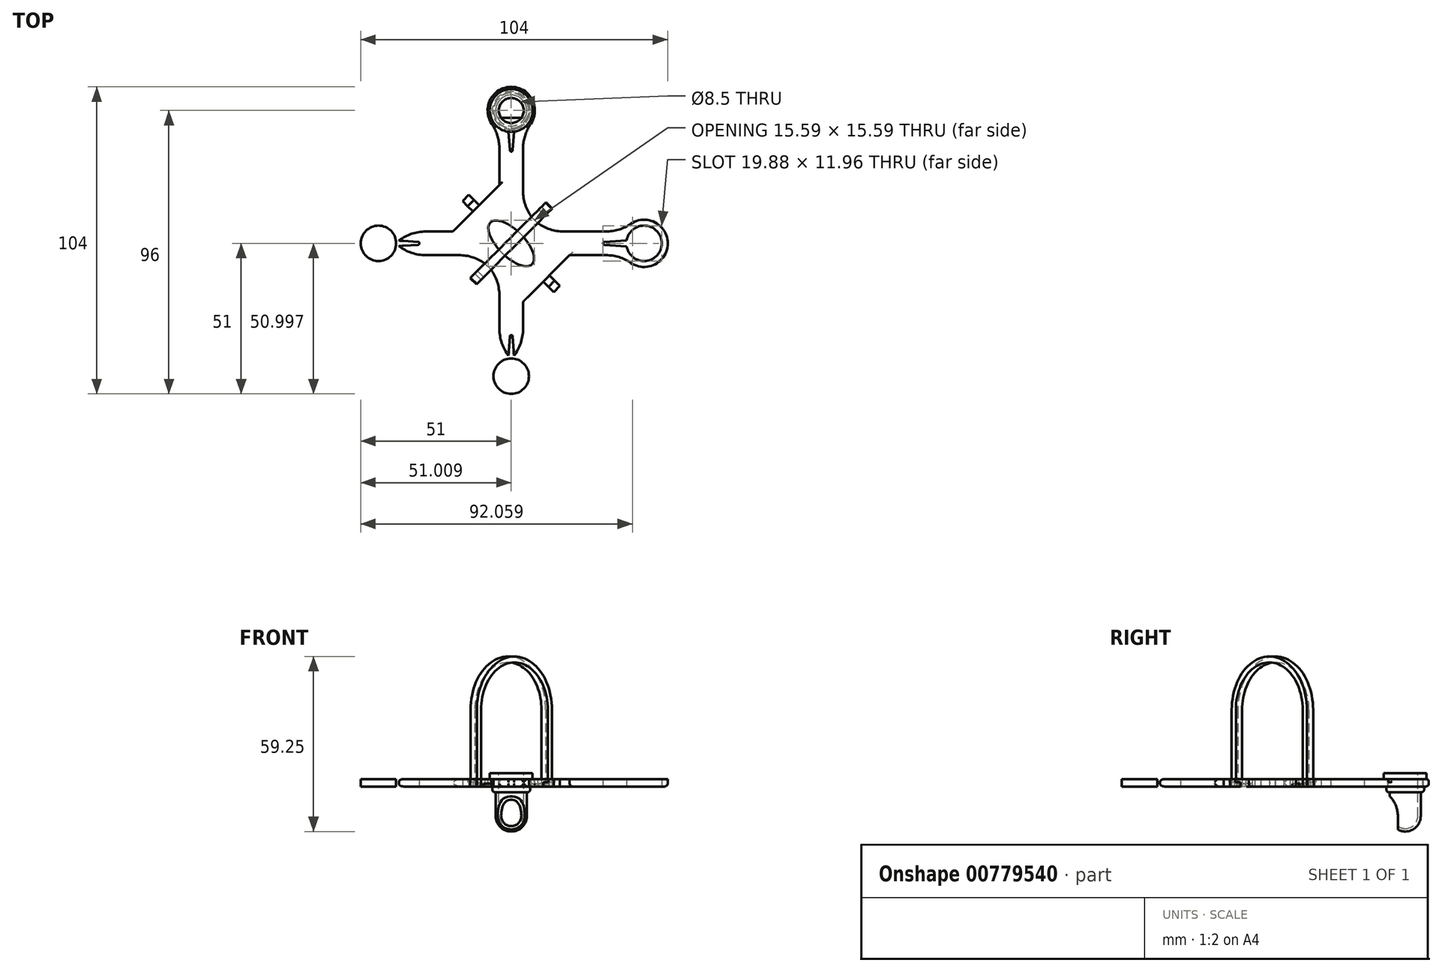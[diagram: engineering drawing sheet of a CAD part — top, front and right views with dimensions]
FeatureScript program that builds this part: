
annotation { "Feature Type Name" : "Feature", "Feature Type Description" : "" }
export const myFeature = defineFeature(function(context is Context, id is Id, definition is map)
    precondition{}
    {
        {
            var Q0;
            Q0=qCreatedBy(makeId("Top.planeOp"),FACE);
            var sketch = newSketch(context, id + "F0", { "sketchPlane" : qUnion([Q0])});
            skPoint(sketch, "E0.center", {"position": v(0, 45) * mm});
            skCircle(sketch, "E1", {"center": v(0, 45) * mm, "radius": 8 * mm});
            skPoint(sketch, "E2.MirrorP", {"position": v(0, -45) * mm});
            skPoint(sketch, "E3.center", {"position": v(-45, 0) * mm});
            skPoint(sketch, "E4.MirrorP", {"position": v(45, 0) * mm});
            skLineSegment(sketch, "E5.bottom", {"start": v(-4, 38.07) * mm, "end": v(4, 38.07) * mm});
            skLineSegment(sketch, "E5.top", {"start": v(-4, -38.07) * mm, "end": v(4, -38.07) * mm});
            skLineSegment(sketch, "E5.left", {"start": v(-4, 38.07) * mm, "end": v(-4, -38.07) * mm});
            skLineSegment(sketch, "E5.right", {"start": v(4, 38.07) * mm, "end": v(4, -38.07) * mm});
            skPoint(sketch, "E5.middle", {"position": v(0, 0) * mm});
            skLineSegment(sketch, "E6.bottom", {"start": v(-38.07, 4) * mm, "end": v(38.07, 4) * mm});
            skLineSegment(sketch, "E6.top", {"start": v(-38.07, -4) * mm, "end": v(38.07, -4) * mm});
            skLineSegment(sketch, "E6.left", {"start": v(-38.07, 4) * mm, "end": v(-38.07, -4) * mm});
            skLineSegment(sketch, "E6.right", {"start": v(38.07, 4) * mm, "end": v(38.07, -4) * mm});
            skCircle(sketch, "E7", {"center": v(0, 45) * mm, "radius": 6 * mm});
            skCircle(sketch, "E8.MirrorC", {"center": v(0, -45) * mm, "radius": 6 * mm});
            skLineSegment(sketch, "E9", {"start": v(-38.9, 38.9) * mm, "end": v(38.9, -38.9) * mm, "construction": true});
            skCircle(sketch, "E10.MirrorC", {"center": v(-45, 0) * mm, "radius": 6 * mm});
            skCircle(sketch, "E11.MirrorC", {"center": v(45, 0) * mm, "radius": 6 * mm});
            skCircle(sketch, "E12.MirrorC", {"center": v(0, -45) * mm, "radius": 8 * mm});
            skCircle(sketch, "E13.MirrorC", {"center": v(-45, 0) * mm, "radius": 8 * mm});
            skCircle(sketch, "E14.MirrorC", {"center": v(45, 0) * mm, "radius": 8 * mm});
            skLineSegment(sketch, "E15", {"start": v(1, 39.08) * mm, "end": v(0, 24.12) * mm});
            skLineSegment(sketch, "E16.MirrorCS", {"start": v(-1, 39.08) * mm, "end": v(0, 24.12) * mm});
            skLineSegment(sketch, "E17.MirrorCS", {"start": v(-1, -39.08) * mm, "end": v(0, -24.12) * mm});
            skLineSegment(sketch, "E18.MirrorCS", {"start": v(1, -39.08) * mm, "end": v(0, -24.12) * mm});
            skLineSegment(sketch, "E19.MirrorCS", {"start": v(-39.08, 1) * mm, "end": v(-24.12, 0) * mm});
            skLineSegment(sketch, "E20.MirrorCS", {"start": v(-39.08, -1) * mm, "end": v(-24.12, 0) * mm});
            skLineSegment(sketch, "E21.MirrorCS", {"start": v(39.08, 1) * mm, "end": v(24.12, 0) * mm});
            skLineSegment(sketch, "E22.MirrorCS", {"start": v(39.08, -1) * mm, "end": v(24.12, 0) * mm});
            skCircle(sketch, "E23", {"center": v(0, 31.62) * mm, "radius": 0.5 * mm});
            skCircle(sketch, "E24.MirrorC", {"center": v(0, -31.62) * mm, "radius": 0.5 * mm});
            skCircle(sketch, "E25.MirrorC", {"center": v(-31.62, 0) * mm, "radius": 0.5 * mm});
            skCircle(sketch, "E26.MirrorC", {"center": v(31.62, 0) * mm, "radius": 0.5 * mm});
            skLineSegment(sketch, "E27", {"start": v(34.68, 34.68) * mm, "end": v(-38.79, -38.79) * mm, "construction": true});
            skSolve(sketch);
        }
        {
            var Q0;
            {var subQ3=sQuery(id+"F0.wireOp",EDGE,"E15");var subQ5=sQuery(id+"F0.wireOp",EDGE,"E7");var subQ6=makeQuery(id+"F0.imprint","INTERSECT",VERTEX,{"derivedFrom":[subQ5,subQ3]});Q0=makeQuery(id+"F0.imprint","IMPRINT",FACE,{"disambiguationData":[TD([[makeQuery(id+"F0.imprint","IMPRINT",EDGE,{"disambiguationData":[TD([[subQ6,-1.0]])],"derivedFrom":subQ5}),-1.0]])]});}
            var Q1;
            {var subQ1=sQuery(id+"F0.wireOp",EDGE,"E1");var subQ3=sQuery(id+"F0.wireOp",EDGE,"E16.MirrorCS");var subQ4=makeQuery(id+"F0.imprint","INTERSECT",VERTEX,{"derivedFrom":[subQ1,subQ3]});Q1=makeQuery(id+"F0.imprint","IMPRINT",FACE,{"disambiguationData":[TD([[makeQuery(id+"F0.imprint","IMPRINT",EDGE,{"disambiguationData":[TD([[subQ4,1.0]])],"derivedFrom":subQ3}),-1.0]])]});}
            var Q2;
            {var subQ1=sQuery(id+"F0.wireOp",EDGE,"E1");var subQ3=sQuery(id+"F0.wireOp",EDGE,"E15");var subQ4=makeQuery(id+"F0.imprint","INTERSECT",VERTEX,{"derivedFrom":[subQ1,subQ3]});Q2=makeQuery(id+"F0.imprint","IMPRINT",FACE,{"disambiguationData":[TD([[makeQuery(id+"F0.imprint","IMPRINT",EDGE,{"disambiguationData":[TD([[subQ4,1.0]])],"derivedFrom":subQ3}),1.0]])]});}
            var Q3;
            {var subQ4=sQuery(id+"F0.wireOp",EDGE,"E6.bottom");var subQ8=sQuery(id+"F0.wireOp",EDGE,"E5.left");var subQ10=makeQuery(id+"F0.imprint","INTERSECT",VERTEX,{"derivedFrom":[subQ8,subQ4]});Q3=makeQuery(id+"F0.imprint","IMPRINT",FACE,{"disambiguationData":[TD([[makeQuery(id+"F0.imprint","IMPRINT",EDGE,{"disambiguationData":[TD([[subQ10,-1.0]])],"derivedFrom":subQ4}),1.0]])]});}
            var Q4;
            {var subQ0=sQuery(id+"F0.wireOp",EDGE,"E16.MirrorCS");var subQ1=sQuery(id+"F0.wireOp",EDGE,"E15");var subQ2=makeQuery(id+"F0.imprint","INTERSECT",VERTEX,{"derivedFrom":[subQ1,subQ0]});Q4=makeQuery(id+"F0.imprint","IMPRINT",FACE,{"disambiguationData":[TD([[makeQuery(id+"F0.imprint","IMPRINT",EDGE,{"disambiguationData":[TD([[subQ2,1.0]])],"derivedFrom":subQ1}),-1.0]])]});}
            var Q5;
            {var subQ4=sQuery(id+"F0.wireOp",EDGE,"E5.right");var subQ6=sQuery(id+"F0.wireOp",EDGE,"E6.bottom");var subQ8=makeQuery(id+"F0.imprint","INTERSECT",VERTEX,{"derivedFrom":[subQ4,subQ6]});Q5=makeQuery(id+"F0.imprint","IMPRINT",FACE,{"disambiguationData":[TD([[makeQuery(id+"F0.imprint","IMPRINT",EDGE,{"disambiguationData":[TD([[subQ8,-1.0]])],"derivedFrom":subQ4}),1.0]])]});}
            var Q6;
            {var subQ4=sQuery(id+"F0.wireOp",EDGE,"E21.MirrorCS");var subQ8=sQuery(id+"F0.wireOp",EDGE,"E11.MirrorC");var subQ10=makeQuery(id+"F0.imprint","INTERSECT",VERTEX,{"derivedFrom":[subQ8,subQ4]});Q6=makeQuery(id+"F0.imprint","IMPRINT",FACE,{"disambiguationData":[TD([[makeQuery(id+"F0.imprint","IMPRINT",EDGE,{"disambiguationData":[TD([[subQ10,1.0]])],"derivedFrom":subQ8}),-1.0]])]});}
            var Q7;
            {var subQ1=sQuery(id+"F0.wireOp",EDGE,"E6.right");var subQ3=sQuery(id+"F0.wireOp",EDGE,"E21.MirrorCS");var subQ4=makeQuery(id+"F0.imprint","INTERSECT",VERTEX,{"derivedFrom":[subQ1,subQ3]});Q7=makeQuery(id+"F0.imprint","IMPRINT",FACE,{"disambiguationData":[TD([[makeQuery(id+"F0.imprint","IMPRINT",EDGE,{"disambiguationData":[TD([[subQ4,-1.0]])],"derivedFrom":subQ3}),-1.0]])]});}
            var Q8;
            {var subQ1=sQuery(id+"F0.wireOp",EDGE,"E6.right");var subQ3=sQuery(id+"F0.wireOp",EDGE,"E22.MirrorCS");var subQ4=makeQuery(id+"F0.imprint","INTERSECT",VERTEX,{"derivedFrom":[subQ1,subQ3]});Q8=makeQuery(id+"F0.imprint","IMPRINT",FACE,{"disambiguationData":[TD([[makeQuery(id+"F0.imprint","IMPRINT",EDGE,{"disambiguationData":[TD([[subQ4,-1.0]])],"derivedFrom":subQ3}),1.0]])]});}
            var Q9;
            {var subQ0=sQuery(id+"F0.wireOp",EDGE,"E6.bottom");var subQ1=sQuery(id+"F0.wireOp",EDGE,"E5.left");var subQ2=makeQuery(id+"F0.imprint","INTERSECT",VERTEX,{"derivedFrom":[subQ1,subQ0]});Q9=makeQuery(id+"F0.imprint","IMPRINT",FACE,{"disambiguationData":[TD([[makeQuery(id+"F0.imprint","IMPRINT",EDGE,{"disambiguationData":[TD([[subQ2,-1.0]])],"derivedFrom":subQ1}),1.0]])]});}
            var Q10;
            {var subQ2=sQuery(id+"F0.wireOp",EDGE,"E6.bottom");var subQ8=sQuery(id+"F0.wireOp",EDGE,"E5.left");var subQ10=makeQuery(id+"F0.imprint","INTERSECT",VERTEX,{"derivedFrom":[subQ8,subQ2]});Q10=makeQuery(id+"F0.imprint","IMPRINT",FACE,{"disambiguationData":[TD([[makeQuery(id+"F0.imprint","IMPRINT",EDGE,{"disambiguationData":[TD([[subQ10,-1.0]])],"derivedFrom":subQ8}),-1.0]])]});}
            var Q11;
            {var subQ0=sQuery(id+"F0.wireOp",EDGE,"E22.MirrorCS");var subQ1=sQuery(id+"F0.wireOp",EDGE,"E21.MirrorCS");var subQ2=makeQuery(id+"F0.imprint","INTERSECT",VERTEX,{"derivedFrom":[subQ1,subQ0]});Q11=makeQuery(id+"F0.imprint","IMPRINT",FACE,{"disambiguationData":[TD([[makeQuery(id+"F0.imprint","IMPRINT",EDGE,{"disambiguationData":[TD([[subQ2,1.0]])],"derivedFrom":subQ1}),1.0]])]});}
            var Q12;
            {var subQ0=sQuery(id+"F0.wireOp",EDGE,"E18.MirrorCS");var subQ1=sQuery(id+"F0.wireOp",EDGE,"E17.MirrorCS");var subQ2=makeQuery(id+"F0.imprint","INTERSECT",VERTEX,{"derivedFrom":[subQ1,subQ0]});Q12=makeQuery(id+"F0.imprint","IMPRINT",FACE,{"disambiguationData":[TD([[makeQuery(id+"F0.imprint","IMPRINT",EDGE,{"disambiguationData":[TD([[subQ2,1.0]])],"derivedFrom":subQ1}),-1.0]])]});}
            var Q13;
            {var subQ1=sQuery(id+"F0.wireOp",EDGE,"E5.left");var subQ8=sQuery(id+"F0.wireOp",EDGE,"E6.top");var subQ9=makeQuery(id+"F0.imprint","INTERSECT",VERTEX,{"derivedFrom":[subQ1,subQ8]});Q13=makeQuery(id+"F0.imprint","IMPRINT",FACE,{"disambiguationData":[TD([[makeQuery(id+"F0.imprint","IMPRINT",EDGE,{"disambiguationData":[TD([[subQ9,-1.0]])],"derivedFrom":subQ8}),-1.0]])]});}
            var Q14;
            {var subQ1=sQuery(id+"F0.wireOp",EDGE,"E5.top");var subQ3=sQuery(id+"F0.wireOp",EDGE,"E18.MirrorCS");var subQ4=makeQuery(id+"F0.imprint","INTERSECT",VERTEX,{"derivedFrom":[subQ1,subQ3]});Q14=makeQuery(id+"F0.imprint","IMPRINT",FACE,{"disambiguationData":[TD([[makeQuery(id+"F0.imprint","IMPRINT",EDGE,{"disambiguationData":[TD([[subQ4,-1.0]])],"derivedFrom":subQ3}),-1.0]])]});}
            var Q15;
            {var subQ1=sQuery(id+"F0.wireOp",EDGE,"E5.top");var subQ3=sQuery(id+"F0.wireOp",EDGE,"E17.MirrorCS");var subQ4=makeQuery(id+"F0.imprint","INTERSECT",VERTEX,{"derivedFrom":[subQ1,subQ3]});Q15=makeQuery(id+"F0.imprint","IMPRINT",FACE,{"disambiguationData":[TD([[makeQuery(id+"F0.imprint","IMPRINT",EDGE,{"disambiguationData":[TD([[subQ4,-1.0]])],"derivedFrom":subQ3}),1.0]])]});}
            var Q16;
            {var subQ0=sQuery(id+"F0.wireOp",EDGE,"E17.MirrorCS");var subQ1=sQuery(id+"F0.wireOp",EDGE,"E8.MirrorC");var subQ2=makeQuery(id+"F0.imprint","INTERSECT",VERTEX,{"derivedFrom":[subQ1,subQ0]});Q16=makeQuery(id+"F0.imprint","IMPRINT",FACE,{"disambiguationData":[TD([[makeQuery(id+"F0.imprint","IMPRINT",EDGE,{"disambiguationData":[TD([[subQ2,1.0]])],"derivedFrom":subQ1}),1.0]])]});}
            var Q17;
            {var subQ4=sQuery(id+"F0.wireOp",EDGE,"E19.MirrorCS");var subQ5=sQuery(id+"F0.wireOp",EDGE,"E10.MirrorC");var subQ6=makeQuery(id+"F0.imprint","INTERSECT",VERTEX,{"derivedFrom":[subQ5,subQ4]});Q17=makeQuery(id+"F0.imprint","IMPRINT",FACE,{"disambiguationData":[TD([[makeQuery(id+"F0.imprint","IMPRINT",EDGE,{"disambiguationData":[TD([[subQ6,1.0]])],"derivedFrom":subQ5}),1.0]])]});}
            var Q18;
            {var subQ1=sQuery(id+"F0.wireOp",EDGE,"E6.left");var subQ3=sQuery(id+"F0.wireOp",EDGE,"E19.MirrorCS");var subQ4=makeQuery(id+"F0.imprint","INTERSECT",VERTEX,{"derivedFrom":[subQ1,subQ3]});Q18=makeQuery(id+"F0.imprint","IMPRINT",FACE,{"disambiguationData":[TD([[makeQuery(id+"F0.imprint","IMPRINT",EDGE,{"disambiguationData":[TD([[subQ4,-1.0]])],"derivedFrom":subQ3}),1.0]])]});}
            var Q19;
            {var subQ1=sQuery(id+"F0.wireOp",EDGE,"E6.left");var subQ3=sQuery(id+"F0.wireOp",EDGE,"E20.MirrorCS");var subQ4=makeQuery(id+"F0.imprint","INTERSECT",VERTEX,{"derivedFrom":[subQ1,subQ3]});Q19=makeQuery(id+"F0.imprint","IMPRINT",FACE,{"disambiguationData":[TD([[makeQuery(id+"F0.imprint","IMPRINT",EDGE,{"disambiguationData":[TD([[subQ4,-1.0]])],"derivedFrom":subQ3}),-1.0]])]});}
            var Q20;
            {var subQ0=sQuery(id+"F0.wireOp",EDGE,"E20.MirrorCS");var subQ1=sQuery(id+"F0.wireOp",EDGE,"E19.MirrorCS");var subQ2=makeQuery(id+"F0.imprint","INTERSECT",VERTEX,{"derivedFrom":[subQ1,subQ0]});Q20=makeQuery(id+"F0.imprint","IMPRINT",FACE,{"disambiguationData":[TD([[makeQuery(id+"F0.imprint","IMPRINT",EDGE,{"disambiguationData":[TD([[subQ2,1.0]])],"derivedFrom":subQ1}),-1.0]])]});}
            extrude(context, id + "F1", {"entities" : qUnion([Q0, Q1, Q2, Q3, Q4, Q5, Q6, Q7, Q8, Q9, Q10, Q11, Q12, Q13, Q14, Q15, Q16, Q17, Q18, Q19, Q20]), "depth" : 2.5 * mm, "offsetDistance" : 25 * mm});
        }
        {
            var Q0;
            Q0=qCreatedBy(makeId("Top.planeOp"),FACE);
            var sketch = newSketch(context, id + "F2", { "sketchPlane" : qUnion([Q0])});
            skLineSegment(sketch, "E28.bottom", {"start": v(-19.8, 4) * mm, "end": v(-4, 19.8) * mm});
            skLineSegment(sketch, "E28.top", {"start": v(4, -19.8) * mm, "end": v(19.8, -4) * mm});
            skLineSegment(sketch, "E28.left", {"start": v(-19.8, 4) * mm, "end": v(4, -19.8) * mm});
            skLineSegment(sketch, "E28.right", {"start": v(-4, 19.8) * mm, "end": v(19.8, -4) * mm});
            skPoint(sketch, "E28.middle", {"position": v(0, 0) * mm});
            skLineSegment(sketch, "E29.bottom", {"start": v(4.24, -18.38) * mm, "end": v(18.38, -4.24) * mm, "construction": true});
            skLineSegment(sketch, "E29.top", {"start": v(-18.38, 4.24) * mm, "end": v(-4.24, 18.38) * mm, "construction": true});
            skLineSegment(sketch, "E29.left", {"start": v(4.24, -18.38) * mm, "end": v(-18.38, 4.24) * mm, "construction": true});
            skLineSegment(sketch, "E29.right", {"start": v(18.38, -4.24) * mm, "end": v(-4.24, 18.38) * mm, "construction": true});
            skLineSegment(sketch, "E30", {"start": v(6.84, 8.96) * mm, "end": v(11.79, 13.9) * mm});
            skLineSegment(sketch, "E31", {"start": v(11.79, 13.9) * mm, "end": v(13.9, 11.79) * mm});
            skLineSegment(sketch, "E32", {"start": v(13.9, 11.79) * mm, "end": v(8.96, 6.84) * mm});
            skLineSegment(sketch, "E33.MirrorCS", {"start": v(-8.96, -6.84) * mm, "end": v(-13.9, -11.79) * mm});
            skLineSegment(sketch, "E34.MirrorCS", {"start": v(-11.79, -13.9) * mm, "end": v(-6.84, -8.96) * mm});
            skLineSegment(sketch, "E35.MirrorCS", {"start": v(-13.9, -11.79) * mm, "end": v(-11.79, -13.9) * mm});
            skLineSegment(sketch, "E36", {"start": v(9.31, 11.43) * mm, "end": v(11.43, 9.31) * mm});
            skLineSegment(sketch, "E37", {"start": v(-11.43, -9.31) * mm, "end": v(-9.31, -11.43) * mm});
            skLineSegment(sketch, "E38", {"start": v(-12.97, 10.83) * mm, "end": v(-16.5, 14.36) * mm});
            skLineSegment(sketch, "E39", {"start": v(-16.5, 14.36) * mm, "end": v(-14.38, 16.48) * mm});
            skLineSegment(sketch, "E40", {"start": v(-14.38, 16.48) * mm, "end": v(-10.85, 12.95) * mm});
            skLineSegment(sketch, "E41", {"start": v(-12.62, 14.72) * mm, "end": v(-14.74, 12.6) * mm});
            skLineSegment(sketch, "E42.MirrorCS", {"start": v(16.48, -14.38) * mm, "end": v(12.95, -10.85) * mm});
            skLineSegment(sketch, "E43.MirrorCS", {"start": v(10.83, -12.97) * mm, "end": v(14.36, -16.5) * mm});
            skLineSegment(sketch, "E44.MirrorCS", {"start": v(14.36, -16.5) * mm, "end": v(16.48, -14.38) * mm});
            skLineSegment(sketch, "E45.MirrorCS", {"start": v(14.72, -12.62) * mm, "end": v(12.6, -14.74) * mm});
            skSolve(sketch);
        }
        {
            var Q0;
            Q0=qSketchRegion(id+"F2",true);
            extrude(context, id + "F3", {"entities" : qUnion([Q0]), "operationType" : NewBodyOperationType.ADD, "depth" : 2.5 * mm, "offsetDistance" : 25 * mm});
        }
        {
            var Q0;
            {var subQ0=sQuery(id+"F0.wireOp",EDGE,"E5.left");var subQ2=sQuery(id+"F0.wireOp",EDGE,"E1");var subQ3=sQuery(id+"F0.wireOp",EDGE,"E6.bottom");var subQ5=sQuery(id+"F0.wireOp",EDGE,"51bbf768-7248-469b-8c03-81a92e2fee1e4.MirrorC");var subQ6=sQuery(id+"F0.wireOp",EDGE,"51bbf768-7248-469b-8c03-81a92e2fee1e3.MirrorC");var subQ7=sQuery(id+"F0.wireOp",EDGE,"51bbf768-7248-469b-8c03-81a92e2fee1e2.MirrorC");var subQ8=sQuery(id+"F0.wireOp",EDGE,"51bbf768-7248-469b-8c03-81a92e2fee1e1.MirrorC");var subQ9=sQuery(id+"F0.wireOp",EDGE,"51bbf768-7248-469b-8c03-81a92e2fee1e0.MirrorC");var subQ10=sQuery(id+"F0.wireOp",EDGE,"19e26025-abd8-4f06-8e8c-6a666a63a616");var subQ11=sQuery(id+"F0.wireOp",EDGE,"598c6ef1-5939-428d-88fe-4b21ed39706e.1.3.0");var subQ12=sQuery(id+"F0.wireOp",EDGE,"E3.2.0");var subQ13=sQuery(id+"F0.wireOp",EDGE,"E3.1.0");var subQ14=sQuery(id+"F0.wireOp",EDGE,"c63fb3b6-9377-47fa-ba11-29589a2d911d");var subQ15=sQuery(id+"F0.wireOp",EDGE,"E0.2.0");var subQ16=sQuery(id+"F0.wireOp",EDGE,"E0.1.0");var subQ17=sQuery(id+"F0.wireOp",EDGE,"1841d06c-6167-486a-ac26-2bc6ea0ff5a3.1.3.0");var subQ19=sQuery(id+"F0.wireOp",EDGE,"20bb631d-0421-4e81-8fba-f625033d7a898.MirrorC");var subQ20=sQuery(id+"F0.wireOp",EDGE,"E6.top");var subQ22=sQuery(id+"F0.wireOp",EDGE,"jg3JzTFg-ilfI-jJIB-Kd6Z-DIGPSq1nITlw");var subQ23=sQuery(id+"F0.wireOp",EDGE,"20bb631d-0421-4e81-8fba-f625033d7a890.MirrorC");var subQ24=sQuery(id+"F0.wireOp",EDGE,"20bb631d-0421-4e81-8fba-f625033d7a891.MirrorC");var subQ25=sQuery(id+"F0.wireOp",EDGE,"20bb631d-0421-4e81-8fba-f625033d7a892.MirrorC");var subQ26=sQuery(id+"F0.wireOp",EDGE,"20bb631d-0421-4e81-8fba-f625033d7a893.MirrorC");var subQ27=sQuery(id+"F0.wireOp",EDGE,"E5.right");var subQ32=sQuery(id+"F2.wireOp",EDGE,"UVMeGlA9-Bkmn-TeG9-sZP4-qDwB2kEt46mr.bottom");var subQ33=sQuery(id+"F2.wireOp",EDGE,"UVMeGlA9-Bkmn-TeG9-sZP4-qDwB2kEt46mr.top");var subQ34=sQuery(id+"F2.wireOp",EDGE,"UVMeGlA9-Bkmn-TeG9-sZP4-qDwB2kEt46mr.left");var subQ35=sQuery(id+"F2.wireOp",EDGE,"UVMeGlA9-Bkmn-TeG9-sZP4-qDwB2kEt46mr.right");Q0=makeQuery(id+"FhcVAunL5KojDzv_1.boolean.opBoolean","SPLIT",FACE,{"disambiguationData":[TD([makeQuery(id+"F1.opExtrude","SWEPT_FACE",FACE,{"disambiguationData":[OSD([subQ22])]})])],"derivedFrom":makeQuery(id+"F3.boolean.opBoolean","MERGE",FACE,{"derivedFrom":[makeQuery(id+"F1.opExtrude","CAP_FACE",FACE,{"disambiguationData":[OSD([subQ22,subQ16,subQ15,subQ17,subQ2,subQ23,subQ24,subQ25,subQ26,subQ19,subQ14,subQ13,subQ12,subQ11,subQ10,subQ9,subQ8,subQ7,subQ6,subQ5,subQ0,subQ27,subQ3,subQ20])],"isStart":false}),makeQuery(id+"F3.opExtrude","CAP_FACE",FACE,{"disambiguationData":[OSD([subQ32,subQ33,subQ34,subQ35])],"isStart":false})]})});}
            var sketch = newSketch(context, id + "F4", { "sketchPlane" : qUnion([Q0])});
            skEllipse(sketch, "E46", {"center": v(0, 0) * mm, "majorRadius": 10 * mm, "minorRadius": 4.5 * mm, "majorAxis": v(-0.7, 0.7)});
            skSolve(sketch);
        }
        {
            var Q0;
            Q0=makeQuery(id+"F4.imprint","IMPRINT",FACE,{"disambiguationData":[TD([[makeQuery(id+"F4.imprint","IMPRINT",EDGE,{"derivedFrom":sQuery(id+"F4.wireOp",EDGE,"E46")}),1.0]])]});
            extrude(context, id + "F5", {"entities" : qUnion([Q0]), "operationType" : NewBodyOperationType.REMOVE, "endBound" : BoundingType.UP_TO_NEXT, "oppositeDirection" : true, "depth" : 25 * mm, "offsetDistance" : 25 * mm});
        }
        {
            var Q0;
            Q0=makeQuery(id+"F3.opExtrude","SWEPT_EDGE",EDGE,{"disambiguationData":[OSD([sQuery(id+"F2.wireOp",EDGE,"E28.top"),sQuery(id+"F2.wireOp",EDGE,"E28.right")])]});
            var Q1;
            Q1=makeQuery(id+"F3.opExtrude","SWEPT_EDGE",EDGE,{"disambiguationData":[OSD([sQuery(id+"F2.wireOp",EDGE,"E28.top"),sQuery(id+"F2.wireOp",EDGE,"E28.left")])]});
            var Q2;
            {var subQ0=sQuery(id+"F0.wireOp",EDGE,"E5.left");Q2=makeQuery(id+"F3.boolean.opBoolean","INTERSECT",EDGE,{"derivedFrom":[makeQuery(id+"F1.opExtrude","SWEPT_FACE",FACE,{"disambiguationData":[OSD([subQ0]),TDD([makeQuery(id+"F0.imprint","IMPRINT",EDGE,{"disambiguationData":[TD([[makeQuery(id+"F0.imprint","INTERSECT",VERTEX,{"derivedFrom":[subQ0,sQuery(id+"F0.wireOp",EDGE,"E6.top")]}),-1.0]])],"derivedFrom":subQ0})])]}),makeQuery(id+"F3.opExtrude","SWEPT_FACE",FACE,{"disambiguationData":[OSD([sQuery(id+"F2.wireOp",EDGE,"E28.left")])]})]});}
            var Q3;
            {var subQ0=sQuery(id+"F0.wireOp",EDGE,"E6.top");Q3=makeQuery(id+"F3.boolean.opBoolean","INTERSECT",EDGE,{"derivedFrom":[makeQuery(id+"F1.opExtrude","SWEPT_FACE",FACE,{"disambiguationData":[OSD([subQ0]),TDD([makeQuery(id+"F0.imprint","IMPRINT",EDGE,{"disambiguationData":[TD([[makeQuery(id+"F0.imprint","INTERSECT",VERTEX,{"derivedFrom":[sQuery(id+"F0.wireOp",EDGE,"E5.left"),subQ0]}),1.0]])],"derivedFrom":subQ0})])]}),makeQuery(id+"F3.opExtrude","SWEPT_FACE",FACE,{"disambiguationData":[OSD([sQuery(id+"F2.wireOp",EDGE,"E28.left")])]})]});}
            var Q4;
            {var subQ0=sQuery(id+"F0.wireOp",EDGE,"E6.bottom");Q4=makeQuery(id+"F3.boolean.opBoolean","INTERSECT",EDGE,{"derivedFrom":[makeQuery(id+"F1.opExtrude","SWEPT_FACE",FACE,{"disambiguationData":[OSD([subQ0]),TDD([makeQuery(id+"F0.imprint","IMPRINT",EDGE,{"disambiguationData":[TD([[makeQuery(id+"F0.imprint","INTERSECT",VERTEX,{"derivedFrom":[sQuery(id+"F0.wireOp",EDGE,"E5.right"),subQ0]}),-1.0]])],"derivedFrom":subQ0})])]}),makeQuery(id+"F3.opExtrude","SWEPT_FACE",FACE,{"disambiguationData":[OSD([sQuery(id+"F2.wireOp",EDGE,"E28.right")])]})]});}
            var Q5;
            {var subQ0=sQuery(id+"F0.wireOp",EDGE,"E5.right");Q5=makeQuery(id+"F3.boolean.opBoolean","INTERSECT",EDGE,{"derivedFrom":[makeQuery(id+"F1.opExtrude","SWEPT_FACE",FACE,{"disambiguationData":[OSD([subQ0]),TDD([makeQuery(id+"F0.imprint","IMPRINT",EDGE,{"disambiguationData":[TD([[makeQuery(id+"F0.imprint","INTERSECT",VERTEX,{"derivedFrom":[subQ0,sQuery(id+"F0.wireOp",EDGE,"E6.bottom")]}),1.0]])],"derivedFrom":subQ0})])]}),makeQuery(id+"F3.opExtrude","SWEPT_FACE",FACE,{"disambiguationData":[OSD([sQuery(id+"F2.wireOp",EDGE,"E28.right")])]})]});}
            var Q6;
            Q6=makeQuery(id+"F3.opExtrude","SWEPT_EDGE",EDGE,{"disambiguationData":[OSD([sQuery(id+"F2.wireOp",EDGE,"E28.bottom"),sQuery(id+"F2.wireOp",EDGE,"E28.right")])]});
            var Q7;
            Q7=makeQuery(id+"F3.opExtrude","SWEPT_EDGE",EDGE,{"disambiguationData":[OSD([sQuery(id+"F2.wireOp",EDGE,"E28.bottom"),sQuery(id+"F2.wireOp",EDGE,"E28.left")])]});
            var Q8;
            Q8=makeQuery(id+"F1.opExtrude","SWEPT_EDGE",EDGE,{"disambiguationData":[OSD([sQuery(id+"F0.wireOp",EDGE,"E5.top"),sQuery(id+"F0.wireOp",EDGE,"E5.left"),sQuery(id+"F0.wireOp",EDGE,"E12.MirrorC")])]});
            var Q9;
            Q9=makeQuery(id+"F1.opExtrude","SWEPT_EDGE",EDGE,{"disambiguationData":[OSD([sQuery(id+"F0.wireOp",EDGE,"E5.top"),sQuery(id+"F0.wireOp",EDGE,"E5.right"),sQuery(id+"F0.wireOp",EDGE,"E12.MirrorC")])]});
            var Q10;
            Q10=makeQuery(id+"F1.opExtrude","SWEPT_EDGE",EDGE,{"disambiguationData":[OSD([sQuery(id+"F0.wireOp",EDGE,"E6.top"),sQuery(id+"F0.wireOp",EDGE,"E6.right"),sQuery(id+"F0.wireOp",EDGE,"E14.MirrorC")])]});
            var Q11;
            Q11=makeQuery(id+"F1.opExtrude","SWEPT_EDGE",EDGE,{"disambiguationData":[OSD([sQuery(id+"F0.wireOp",EDGE,"E6.bottom"),sQuery(id+"F0.wireOp",EDGE,"E6.right"),sQuery(id+"F0.wireOp",EDGE,"E14.MirrorC")])]});
            var Q12;
            Q12=makeQuery(id+"F1.opExtrude","SWEPT_EDGE",EDGE,{"disambiguationData":[OSD([sQuery(id+"F0.wireOp",EDGE,"E1"),sQuery(id+"F0.wireOp",EDGE,"E5.bottom"),sQuery(id+"F0.wireOp",EDGE,"E5.right")])]});
            var Q13;
            Q13=makeQuery(id+"F1.opExtrude","SWEPT_EDGE",EDGE,{"disambiguationData":[OSD([sQuery(id+"F0.wireOp",EDGE,"E1"),sQuery(id+"F0.wireOp",EDGE,"E5.bottom"),sQuery(id+"F0.wireOp",EDGE,"E5.left")])]});
            var Q14;
            Q14=makeQuery(id+"F1.opExtrude","SWEPT_EDGE",EDGE,{"disambiguationData":[OSD([sQuery(id+"F0.wireOp",EDGE,"E6.top"),sQuery(id+"F0.wireOp",EDGE,"E6.left"),sQuery(id+"F0.wireOp",EDGE,"E13.MirrorC")])]});
            var Q15;
            Q15=makeQuery(id+"F1.opExtrude","SWEPT_EDGE",EDGE,{"disambiguationData":[OSD([sQuery(id+"F0.wireOp",EDGE,"E6.bottom"),sQuery(id+"F0.wireOp",EDGE,"E6.left"),sQuery(id+"F0.wireOp",EDGE,"E13.MirrorC")])]});
            fillet(context, id + "F6", {"entities" : qUnion([Q0, Q1, Q2, Q3, Q4, Q5, Q6, Q7, Q8, Q9, Q10, Q11, Q12, Q13, Q14, Q15]), "radius" : 15 * mm, "tangentPropagation" : true, "allowEdgeOverflow" : false});
        }
        {
            var Q0;
            {var subQ5=sQuery(id+"F2.wireOp",EDGE,"E41");Q0=makeQuery(id+"F2.imprint","IMPRINT",FACE,{"disambiguationData":[TD([[makeQuery(id+"F2.imprint","IMPRINT",EDGE,{"derivedFrom":subQ5}),1.0]])]});}
            var Q1;
            {var subQ5=sQuery(id+"F2.wireOp",EDGE,"E45.MirrorCS");Q1=makeQuery(id+"F2.imprint","IMPRINT",FACE,{"disambiguationData":[TD([[makeQuery(id+"F2.imprint","IMPRINT",EDGE,{"derivedFrom":subQ5}),-1.0]])]});}
            extrude(context, id + "F7", {"entities" : qUnion([Q0, Q1]), "operationType" : NewBodyOperationType.REMOVE, "depth" : 3 * mm, "offsetDistance" : 25 * mm, "hasSecondDirection" : true, "secondDirectionOppositeDirection" : false, "secondDirectionDepth" : 1.5 * mm});
        }
        {
            var Q0;
            {var subQ0=sQuery(id+"F2.wireOp",EDGE,"E28.bottom");var subQ1=sQuery(id+"F2.wireOp",EDGE,"E34.MirrorCS");var subQ2=sQuery(id+"F2.wireOp",EDGE,"E28.left");var subQ3=sQuery(id+"F0.wireOp",EDGE,"E14.MirrorC");var subQ4=sQuery(id+"F2.wireOp",EDGE,"E32");var subQ5=sQuery(id+"F0.wireOp",EDGE,"E13.MirrorC");var subQ6=sQuery(id+"F2.wireOp",EDGE,"E30");var subQ7=sQuery(id+"F0.wireOp",EDGE,"E12.MirrorC");var subQ8=sQuery(id+"F2.wireOp",EDGE,"E35.MirrorCS");var subQ9=sQuery(id+"F2.wireOp",EDGE,"E33.MirrorCS");var subQ10=sQuery(id+"F2.wireOp",EDGE,"E31");var subQ11=sQuery(id+"F2.wireOp",EDGE,"E28.right");var subQ12=sQuery(id+"F2.wireOp",EDGE,"E28.top");var subQ13=sQuery(id+"F0.wireOp",EDGE,"E11.MirrorC");var subQ14=sQuery(id+"F0.wireOp",EDGE,"E10.MirrorC");var subQ15=sQuery(id+"F0.wireOp",EDGE,"E8.MirrorC");var subQ16=sQuery(id+"F0.wireOp",EDGE,"E7");var subQ17=sQuery(id+"F0.wireOp",EDGE,"E6.top");var subQ18=sQuery(id+"F0.wireOp",EDGE,"E6.bottom");var subQ19=sQuery(id+"F0.wireOp",EDGE,"E5.right");var subQ20=sQuery(id+"F0.wireOp",EDGE,"E5.left");var subQ21=sQuery(id+"F0.wireOp",EDGE,"E1");var subQ22=makeQuery(id+"F3.boolean.opBoolean","MERGE",FACE,{"derivedFrom":[makeQuery(id+"F1.opExtrude","CAP_FACE",FACE,{"disambiguationData":[OSD([subQ21,subQ20,subQ19,subQ18,subQ17,subQ16,subQ15,subQ14,subQ13,subQ7,subQ5,subQ3])],"isStart":false}),makeQuery(id+"F3.opExtrude","CAP_FACE",FACE,{"disambiguationData":[OSD([subQ0,subQ12,subQ2,subQ11,subQ6,subQ10,subQ4,subQ9,subQ1,subQ8])],"isStart":false})]});Q0=makeQuery(id+"F7.boolean.opBoolean","SPLIT",FACE,{"disambiguationData":[TD([makeQuery(id+"F1.opExtrude","SWEPT_FACE",FACE,{"disambiguationData":[OSD([subQ16])]})])],"derivedFrom":subQ22});}
            var sketch = newSketch(context, id + "F8", { "sketchPlane" : qUnion([Q0])});
            skPoint(sketch, "E47.centerSnap0", {"position": v(0, 53) * mm});
            skCircle(sketch, "E48", {"center": v(0, 45) * mm, "radius": 5.9 * mm});
            skCircle(sketch, "E49", {"center": v(0, 45) * mm, "radius": 7.25 * mm});
            skCircle(sketch, "E50", {"center": v(0, 45) * mm, "radius": 4.25 * mm});
            skCircle(sketch, "E51", {"center": v(0, 45) * mm, "radius": 6.4 * mm});
            skSolve(sketch);
        }
        {
            var Q0;
            Q0=makeQuery(id+"F8.imprint","IMPRINT",FACE,{"disambiguationData":[TD([[makeQuery(id+"F8.imprint","IMPRINT",EDGE,{"derivedFrom":sQuery(id+"F8.wireOp",EDGE,"E48")}),1.0]])]});
            extrude(context, id + "F9", {"entities" : qUnion([Q0]), "oppositeDirection" : true, "depth" : 4.5 * mm, "offsetDistance" : 25 * mm});
        }
        {
            var Q0;
            Q0=makeQuery(id+"F8.imprint","IMPRINT",FACE,{"disambiguationData":[TD([[makeQuery(id+"F8.imprint","IMPRINT",EDGE,{"derivedFrom":sQuery(id+"F8.wireOp",EDGE,"E48")}),1.0]])]});
            var Q1;
            {var subQ5=makeQuery(id+"F1.opExtrude","CAP_EDGE",EDGE,{"disambiguationData":[OSD([sQuery(id+"F0.wireOp",EDGE,"E7")])],"isStart":false});Q1=makeQuery(id+"F8.imprint","IMPRINT",FACE,{"disambiguationData":[TD([[makeQuery(id+"F8.imprint","IMPRINT",EDGE,{"derivedFrom":subQ5}),-1.0]])]});}
            var Q2;
            Q2=makeQuery(id+"F8.imprint","IMPRINT",FACE,{"disambiguationData":[TD([[makeQuery(id+"F8.imprint","IMPRINT",EDGE,{"derivedFrom":sQuery(id+"F8.wireOp",EDGE,"E48")}),-1.0]])]});
            var Q3;
            {var subQ0=sQuery(id+"F8.wireOp",EDGE,"E49");var subQ1=makeQuery(id+"F1.opExtrude","CAP_EDGE",EDGE,{"disambiguationData":[OSD([sQuery(id+"F0.wireOp",EDGE,"E15")])],"isStart":false});var subQ2=makeQuery(id+"F8.imprint","INTERSECT",VERTEX,{"derivedFrom":[subQ1,subQ0]});Q3=makeQuery(id+"F8.imprint","IMPRINT",FACE,{"disambiguationData":[TD([[makeQuery(id+"F8.imprint","IMPRINT",EDGE,{"disambiguationData":[TD([[subQ2,-1.0]])],"derivedFrom":subQ0}),1.0]])]});}
            var Q4;
            {var subQ0=sQuery(id+"F8.wireOp",EDGE,"E49");var subQ1=makeQuery(id+"F1.opExtrude","CAP_EDGE",EDGE,{"disambiguationData":[OSD([sQuery(id+"F0.wireOp",EDGE,"E15")])],"isStart":false});var subQ2=makeQuery(id+"F8.imprint","INTERSECT",VERTEX,{"derivedFrom":[subQ1,subQ0]});Q4=makeQuery(id+"F8.imprint","IMPRINT",FACE,{"disambiguationData":[TD([[makeQuery(id+"F8.imprint","IMPRINT",EDGE,{"disambiguationData":[TD([[subQ2,1.0]])],"derivedFrom":subQ0}),1.0]])]});}
            extrude(context, id + "F10", {"entities" : qUnion([Q0, Q1, Q2, Q3, Q4]), "operationType" : NewBodyOperationType.ADD, "depth" : 2 * mm, "offsetDistance" : 25 * mm});
        }
        {
            var Q0;
            {var subQ5=makeQuery(id+"F1.opExtrude","CAP_EDGE",EDGE,{"disambiguationData":[OSD([sQuery(id+"F0.wireOp",EDGE,"E7")])],"isStart":false});Q0=makeQuery(id+"F8.imprint","IMPRINT",FACE,{"disambiguationData":[TD([[makeQuery(id+"F8.imprint","IMPRINT",EDGE,{"derivedFrom":subQ5}),-1.0]])]});}
            var Q1;
            Q1=makeQuery(id+"F8.imprint","IMPRINT",FACE,{"disambiguationData":[TD([[makeQuery(id+"F8.imprint","IMPRINT",EDGE,{"derivedFrom":sQuery(id+"F8.wireOp",EDGE,"E48")}),-1.0]])]});
            extrude(context, id + "F11", {"entities" : qUnion([Q0, Q1]), "operationType" : NewBodyOperationType.ADD, "oppositeDirection" : true, "depth" : 4.5 * mm, "offsetDistance" : 25 * mm, "hasSecondDirection" : true, "secondDirectionOppositeDirection" : true, "secondDirectionDepth" : 2.5 * mm});
        }
        {
            var Q0;
            Q0=qCreatedBy(makeId("Right.planeOp"),FACE);
            var sketch = newSketch(context, id + "F12", { "sketchPlane" : qUnion([Q0])});
            skArc(sketch, "E52", {"start": v(40.75, -10) * mm, "mid": v(42, -13) * mm, "end": v(45, -14.25) * mm});
            skLineSegment(sketch, "E53", {"start": v(40.75, -2) * mm, "end": v(40.75, -10) * mm});
            skArc(sketch, "E54.0", {"start": v(39.75, -10) * mm, "mid": v(41.29, -13.71) * mm, "end": v(45, -15.25) * mm});
            skLineSegment(sketch, "E54.1", {"start": v(39.75, -2) * mm, "end": v(39.75, -10) * mm});
            skLineSegment(sketch, "E55", {"start": v(45, -14.25) * mm, "end": v(45, -15.25) * mm});
            skLineSegment(sketch, "E56", {"start": v(45, -15.25) * mm, "end": v(45, 0) * mm, "construction": true});
            skLineSegment(sketch, "E57", {"start": v(39.75, -2) * mm, "end": v(40.75, -2) * mm});
            skSolve(sketch);
        }
        {
            var Q0;
            {var subQ0=sQuery(id+"F0.wireOp",EDGE,"E5.right");Q0=makeQuery(id+"F1.opExtrude","SWEPT_FACE",FACE,{"disambiguationData":[OSD([subQ0]),TDD([makeQuery(id+"F0.imprint","IMPRINT",EDGE,{"disambiguationData":[TD([[makeQuery(id+"F0.imprint","INTERSECT",VERTEX,{"derivedFrom":[subQ0,sQuery(id+"F0.wireOp",EDGE,"E6.top")]}),-1.0]])],"derivedFrom":subQ0})])]});}
            var Q1;
            {var subQ0=sQuery(id+"F0.wireOp",EDGE,"E5.left");Q1=makeQuery(id+"F1.opExtrude","SWEPT_FACE",FACE,{"disambiguationData":[OSD([subQ0]),TDD([makeQuery(id+"F0.imprint","IMPRINT",EDGE,{"disambiguationData":[TD([[makeQuery(id+"F0.imprint","INTERSECT",VERTEX,{"derivedFrom":[subQ0,sQuery(id+"F0.wireOp",EDGE,"E6.top")]}),-1.0]])],"derivedFrom":subQ0})])]});}
            var Q2;
            {var subQ0=sQuery(id+"F0.wireOp",EDGE,"E6.top");Q2=makeQuery(id+"F1.opExtrude","SWEPT_FACE",FACE,{"disambiguationData":[OSD([subQ0]),TDD([makeQuery(id+"F0.imprint","IMPRINT",EDGE,{"disambiguationData":[TD([[makeQuery(id+"F0.imprint","INTERSECT",VERTEX,{"derivedFrom":[sQuery(id+"F0.wireOp",EDGE,"E5.left"),subQ0]}),1.0]])],"derivedFrom":subQ0})])]});}
            var Q3;
            {var subQ0=sQuery(id+"F0.wireOp",EDGE,"E6.bottom");Q3=makeQuery(id+"F1.opExtrude","SWEPT_FACE",FACE,{"disambiguationData":[OSD([subQ0]),TDD([makeQuery(id+"F0.imprint","IMPRINT",EDGE,{"disambiguationData":[TD([[makeQuery(id+"F0.imprint","INTERSECT",VERTEX,{"derivedFrom":[sQuery(id+"F0.wireOp",EDGE,"E5.left"),subQ0]}),1.0]])],"derivedFrom":subQ0})])]});}
            var Q4;
            {var subQ0=sQuery(id+"F0.wireOp",EDGE,"E5.right");Q4=makeQuery(id+"F1.opExtrude","SWEPT_FACE",FACE,{"disambiguationData":[OSD([subQ0]),TDD([makeQuery(id+"F0.imprint","IMPRINT",EDGE,{"disambiguationData":[TD([[makeQuery(id+"F0.imprint","INTERSECT",VERTEX,{"derivedFrom":[subQ0,sQuery(id+"F0.wireOp",EDGE,"E6.bottom")]}),1.0]])],"derivedFrom":subQ0})])]});}
            var Q5;
            {var subQ0=sQuery(id+"F0.wireOp",EDGE,"E6.bottom");Q5=makeQuery(id+"F1.opExtrude","CAP_EDGE",EDGE,{"disambiguationData":[OSD([subQ0]),TDD([makeQuery(id+"F0.imprint","IMPRINT",EDGE,{"disambiguationData":[TD([[makeQuery(id+"F0.imprint","INTERSECT",VERTEX,{"derivedFrom":[sQuery(id+"F0.wireOp",EDGE,"E5.right"),subQ0]}),-1.0]])],"derivedFrom":subQ0})])],"isStart":true});}
            var Q6;
            Q6=makeQuery(id+"F5.boolean.opBoolean","COPY",FACE,{"derivedFrom":makeQuery(id+"F5.opExtrude","SWEPT_FACE",FACE,{"disambiguationData":[OSD([sQuery(id+"F4.wireOp",EDGE,"E46")])]})});
            var Q7;
            Q7=makeQuery(id+"F11.opExtrude","CAP_EDGE",EDGE,{"disambiguationData":[OSD([sQuery(id+"F8.wireOp",EDGE,"E51")])],"isStart":false});
            var Q8;
            Q8=makeQuery(id+"F11.opExtrude","CAP_EDGE",EDGE,{"disambiguationData":[OSD([sQuery(id+"F8.wireOp",EDGE,"E48")])],"isStart":true});
            fillet(context, id + "F13", {"entities" : qUnion([Q0, Q1, Q2, Q3, Q4, Q5, Q6, Q7, Q8]), "radius" : 1 * mm, "tangentPropagation" : true, "allowEdgeOverflow" : false});
        }
        {
            var Q0;
            Q0=makeQuery(id+"F12.imprint","IMPRINT",FACE,{"disambiguationData":[TD([[makeQuery(id+"F12.imprint","IMPRINT",EDGE,{"derivedFrom":sQuery(id+"F12.wireOp",EDGE,"E52")}),-1.0]])]});
            var Q1;
            Q1=sQuery(id+"F12.wireOp",EDGE,"E56");
            revolve(context, id + "F14", {"operationType" : NewBodyOperationType.ADD, "surfaceOperationType" : NewSurfaceOperationType.NEW, "entities" : qUnion([Q0]), "axis" : qUnion([Q1]), "revolveType" : RevolveType.FULL});
        }
        {
            var Q0;
            {var subQ5=sQuery(id+"F2.wireOp",EDGE,"E37");Q0=makeQuery(id+"F2.imprint","IMPRINT",FACE,{"disambiguationData":[TD([[makeQuery(id+"F2.imprint","IMPRINT",EDGE,{"derivedFrom":subQ5}),1.0]])]});}
            var Q1;
            {var subQ5=sQuery(id+"F2.wireOp",EDGE,"E36");Q1=makeQuery(id+"F2.imprint","IMPRINT",FACE,{"disambiguationData":[TD([[makeQuery(id+"F2.imprint","IMPRINT",EDGE,{"derivedFrom":subQ5}),-1.0]])]});}
            extrude(context, id + "F15", {"entities" : qUnion([Q0, Q1]), "operationType" : NewBodyOperationType.REMOVE, "depth" : 1 * mm, "offsetDistance" : 25 * mm});
        }
        {
            var Q0;
            Q0=sQuery(id+"F0.wireOp",EDGE,"E9");
            cPlane(context, id + "F16", {"entities" : qUnion([Q0]), "cplaneType" : CPlaneType.MID_PLANE, "offset" : 25 * mm, "width" : 150 * mm, "height" : 150 * mm});
        }
        {
            var Q0;
            Q0=qCreatedBy(id+"F16.planeOp",FACE);
            var sketch = newSketch(context, id + "F17", { "sketchPlane" : qUnion([Q0])});
            skArc(sketch, "E58", {"start": v(16, 26) * mm, "mid": v(0, 42) * mm, "end": v(-16, 26) * mm});
            skLineSegment(sketch, "E59", {"start": v(-16, 26) * mm, "end": v(-16, 0) * mm});
            skLineSegment(sketch, "E60", {"start": v(16, 26) * mm, "end": v(16, 0) * mm});
            skArc(sketch, "E61", {"start": v(18, 26) * mm, "mid": v(0, 44) * mm, "end": v(-18, 26) * mm});
            skLineSegment(sketch, "E62", {"start": v(-18, 26) * mm, "end": v(-18, 0) * mm});
            skLineSegment(sketch, "E63", {"start": v(18, 26) * mm, "end": v(18, 0) * mm});
            skLineSegment(sketch, "E64", {"start": v(-18, 0) * mm, "end": v(-16, 0) * mm});
            skLineSegment(sketch, "E65", {"start": v(16, 0) * mm, "end": v(18, 0) * mm});
            skSolve(sketch);
        }
        {
            var Q0;
            Q0=makeQuery(id+"F17.imprint","IMPRINT",FACE,{"disambiguationData":[TD([[makeQuery(id+"F17.imprint","IMPRINT",EDGE,{"derivedFrom":sQuery(id+"F17.wireOp",EDGE,"E58")}),-1.0]])]});
            extrude(context, id + "F18", {"entities" : qUnion([Q0]), "endBound" : BoundingType.SYMMETRIC, "oppositeDirection" : true, "depth" : 3 * mm, "offsetDistance" : 25 * mm});
        }
        {
            var Q0;
            Q0=qCreatedBy(makeId("Right.planeOp"),FACE);
            var sketch = newSketch(context, id + "F19", { "sketchPlane" : qUnion([Q0])});
            skCircle(sketch, "E66", {"center": v(33, -10) * mm, "radius": 9.5 * mm});
            skLineSegment(sketch, "E67", {"start": v(42.5, -19.5) * mm, "end": v(33, -19.5) * mm});
            skLineSegment(sketch, "E68", {"start": v(42.5, -19.5) * mm, "end": v(42.5, -10) * mm});
            skSolve(sketch);
        }
        {
            var Q0;
            Q0=makeQuery(id+"F19.imprint","IMPRINT",FACE,{"disambiguationData":[TD([[makeQuery(id+"F19.imprint","IMPRINT",EDGE,{"derivedFrom":sQuery(id+"F19.wireOp",EDGE,"E66")}),1.0]])]});
            var Q1;
            {var subQ0=sQuery(id+"F19.wireOp",EDGE,"E67");Q1=makeQuery(id+"F19.imprint","IMPRINT",FACE,{"disambiguationData":[TD([[makeQuery(id+"F19.imprint","IMPRINT",EDGE,{"derivedFrom":subQ0}),-1.0]])]});}
            extrude(context, id + "F20", {"entities" : qUnion([Q0, Q1]), "operationType" : NewBodyOperationType.REMOVE, "endBound" : BoundingType.SYMMETRIC, "oppositeDirection" : true, "depth" : 25 * mm, "offsetDistance" : 25 * mm});
        }
    });
